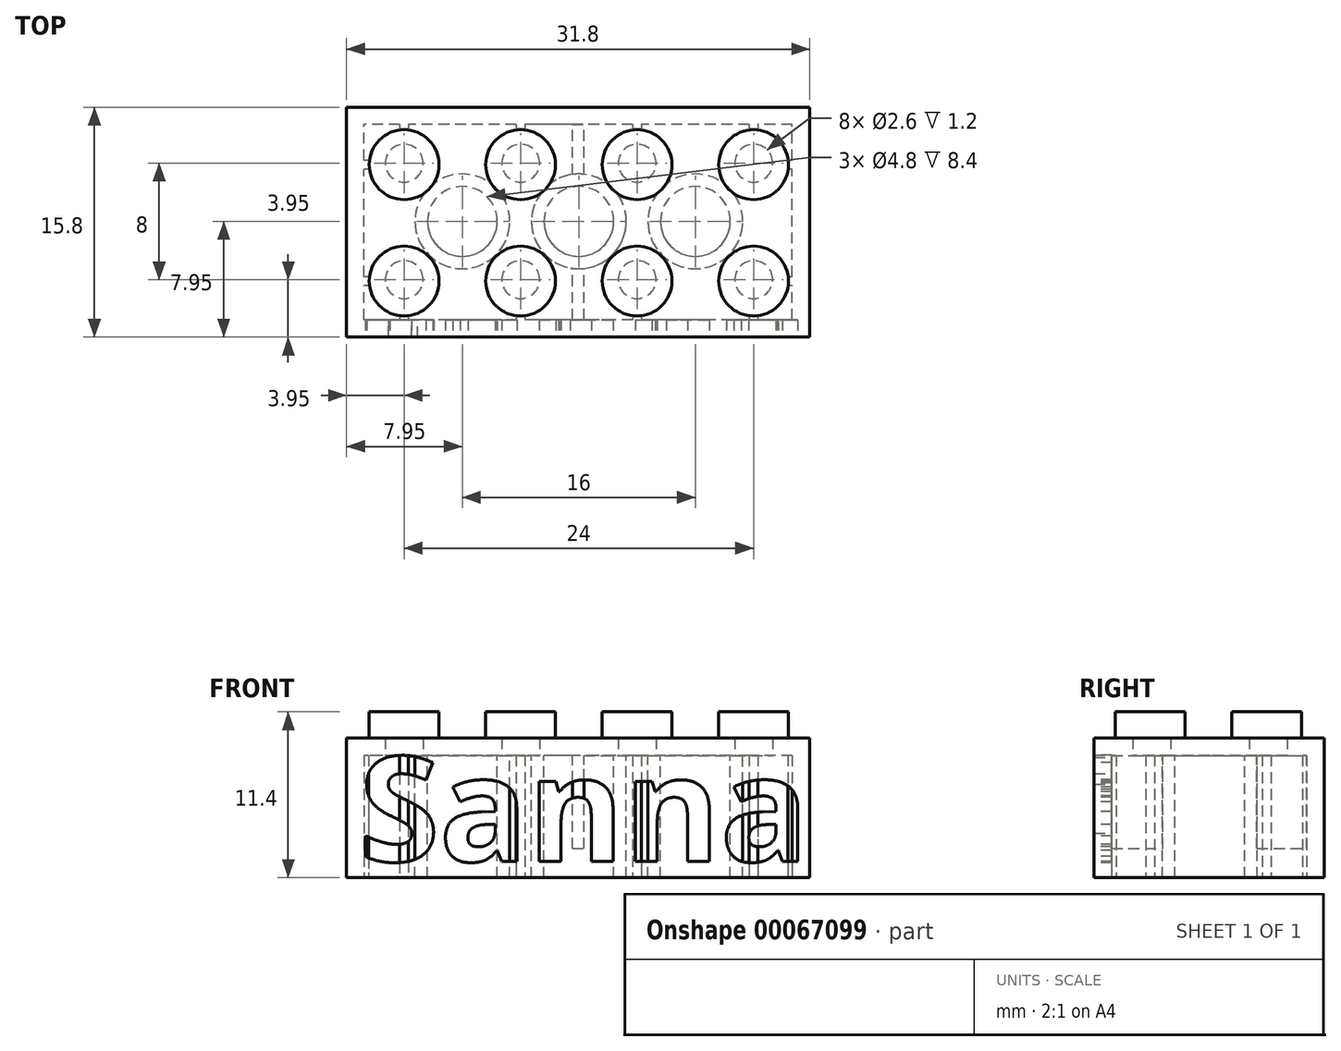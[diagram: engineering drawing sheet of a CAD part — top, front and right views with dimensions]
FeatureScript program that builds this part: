
annotation { "Feature Type Name" : "Feature", "Feature Type Description" : "" }
export const myFeature = defineFeature(function(context is Context, id is Id, definition is map)
    precondition{}
    {
        {
            var Q0;
            Q0=qCreatedBy(makeId("Top.planeOp"),FACE);
            var sketch = newSketch(context, id + "F0", { "sketchPlane" : qUnion([Q0])});
            skLineSegment(sketch, "E0.rect.bottom", {"start": v(15.9, 7.9) * mm, "end": v(-15.9, 7.9) * mm});
            skLineSegment(sketch, "E0.rect.top", {"start": v(15.9, -7.9) * mm, "end": v(-15.9, -7.9) * mm});
            skLineSegment(sketch, "E0.rect.left", {"start": v(15.9, 7.9) * mm, "end": v(15.9, -7.9) * mm});
            skLineSegment(sketch, "E0.rect.right", {"start": v(-15.9, 7.9) * mm, "end": v(-15.9, -7.9) * mm});
            skPoint(sketch, "E0.rect.middle", {"position": v(0, 0) * mm});
            skSolve(sketch);
        }
        {
            var Q0;
            Q0 = qSketchRegion(id + "F0", true);
            extrude(context, id + "F1", {"entities" : qUnion([Q0]), "depth" : 9.6 * mm});
        }
        {
            var Q0;
            Q0=makeQuery(id+"F1.opExtrude","CAP_FACE",FACE,{"disambiguationData":[OSD([sQuery(id+"F0.wireOp",EDGE,"E0.rect.bottom"),sQuery(id+"F0.wireOp",EDGE,"E0.rect.top"),sQuery(id+"F0.wireOp",EDGE,"E0.rect.left"),sQuery(id+"F0.wireOp",EDGE,"E0.rect.right")])],"isStart":true});
            var sketch = newSketch(context, id + "F2", { "sketchPlane" : qUnion([Q0])});
            skLineSegment(sketch, "E1.rect.bottom", {"start": v(14.7, 6.7) * mm, "end": v(-14.7, 6.7) * mm});
            skLineSegment(sketch, "E1.rect.top", {"start": v(14.7, -6.7) * mm, "end": v(-14.7, -6.7) * mm});
            skLineSegment(sketch, "E1.rect.left", {"start": v(14.7, 6.7) * mm, "end": v(14.7, -6.7) * mm});
            skLineSegment(sketch, "E1.rect.right", {"start": v(-14.7, 6.7) * mm, "end": v(-14.7, -6.7) * mm});
            skPoint(sketch, "E1.rect.middle", {"position": v(0, 0) * mm});
            skSolve(sketch);
        }
        {
            var Q0;
            Q0 = qSketchRegion(id + "F2", true);
            extrude(context, id + "F3", {"entities" : qUnion([Q0]), "operationType" : NewBodyOperationType.REMOVE, "oppositeDirection" : true, "depth" : 8.4 * mm});
        }
        {
            var Q0;
            Q0=makeQuery(id+"F1.opExtrude","CAP_FACE",FACE,{"disambiguationData":[OSD([sQuery(id+"F0.wireOp",EDGE,"E0.rect.bottom"),sQuery(id+"F0.wireOp",EDGE,"E0.rect.top"),sQuery(id+"F0.wireOp",EDGE,"E0.rect.left"),sQuery(id+"F0.wireOp",EDGE,"E0.rect.right")])],"isStart":false});
            var sketch = newSketch(context, id + "F4", { "sketchPlane" : qUnion([Q0])});
            skCircle(sketch, "E2", {"center": v(-11.95, 3.95) * mm, "radius": 2.4 * mm});
            skCircle(sketch, "E3.0.1.0", {"center": v(-11.95, -4.05) * mm, "radius": 2.4 * mm});
            skCircle(sketch, "E3.1.0.0", {"center": v(-3.95, 3.95) * mm, "radius": 2.4 * mm});
            skCircle(sketch, "E3.1.1.0", {"center": v(-3.95, -4.05) * mm, "radius": 2.4 * mm});
            skCircle(sketch, "E3.2.0.0", {"center": v(4.05, 3.95) * mm, "radius": 2.4 * mm});
            skCircle(sketch, "E3.2.1.0", {"center": v(4.05, -4.05) * mm, "radius": 2.4 * mm});
            skCircle(sketch, "E3.3.0.0", {"center": v(12.05, 3.95) * mm, "radius": 2.4 * mm});
            skCircle(sketch, "E3.3.1.0", {"center": v(12.05, -4.05) * mm, "radius": 2.4 * mm});
            skLineSegment(sketch, "E3.direction1", {"start": v(-11.95, 3.95) * mm, "end": v(-3.95, 3.95) * mm, "construction": true});
            skLineSegment(sketch, "E3.direction2", {"start": v(-11.95, 3.95) * mm, "end": v(-11.95, -4.05) * mm, "construction": true});
            skLineSegment(sketch, "E4", {"start": v(-23.88, 0) * mm, "end": v(20.47, 0) * mm, "construction": true});
            skSolve(sketch);
        }
        {
            var Q0;
            Q0 = qSketchRegion(id + "F4", true);
            extrude(context, id + "F5", {"entities" : qUnion([Q0]), "operationType" : NewBodyOperationType.ADD, "depth" : 1.8 * mm});
        }
        {
            var Q0;
            Q0=makeQuery(id+"F3.boolean.opBoolean","COPY",FACE,{"derivedFrom":makeQuery(id+"F3.opExtrude","CAP_FACE",FACE,{"disambiguationData":[OSD([sQuery(id+"F2.wireOp",EDGE,"E1.rect.bottom"),sQuery(id+"F2.wireOp",EDGE,"E1.rect.top"),sQuery(id+"F2.wireOp",EDGE,"E1.rect.left"),sQuery(id+"F2.wireOp",EDGE,"E1.rect.right")])],"isStart":false})});
            var sketch = newSketch(context, id + "F6", { "sketchPlane" : qUnion([Q0])});
            skCircle(sketch, "E5", {"center": v(-11.95, 3.95) * mm, "radius": 1.3 * mm});
            skCircle(sketch, "E6.0.1.0", {"center": v(-11.95, -4.05) * mm, "radius": 1.3 * mm});
            skCircle(sketch, "E6.1.0.0", {"center": v(-3.95, 3.95) * mm, "radius": 1.3 * mm});
            skCircle(sketch, "E6.1.1.0", {"center": v(-3.95, -4.05) * mm, "radius": 1.3 * mm});
            skCircle(sketch, "E6.2.0.0", {"center": v(4.05, 3.95) * mm, "radius": 1.3 * mm});
            skCircle(sketch, "E6.2.1.0", {"center": v(4.05, -4.05) * mm, "radius": 1.3 * mm});
            skCircle(sketch, "E6.3.0.0", {"center": v(12.05, 3.95) * mm, "radius": 1.3 * mm});
            skCircle(sketch, "E6.3.1.0", {"center": v(12.05, -4.05) * mm, "radius": 1.3 * mm});
            skLineSegment(sketch, "E6.direction1", {"start": v(-11.95, 3.95) * mm, "end": v(-3.95, 3.95) * mm, "construction": true});
            skLineSegment(sketch, "E6.direction2", {"start": v(-11.95, 3.95) * mm, "end": v(-11.95, -4.05) * mm, "construction": true});
            skSolve(sketch);
        }
        {
            var Q0;
            Q0 = qSketchRegion(id + "F6", true);
            extrude(context, id + "F7", {"entities" : qUnion([Q0]), "operationType" : NewBodyOperationType.REMOVE, "oppositeDirection" : true, "depth" : 1.2 * mm});
        }
        {
            var Q0;
            Q0=makeQuery(id+"F3.boolean.opBoolean","COPY",FACE,{"derivedFrom":makeQuery(id+"F3.opExtrude","CAP_FACE",FACE,{"disambiguationData":[OSD([sQuery(id+"F2.wireOp",EDGE,"E1.rect.bottom"),sQuery(id+"F2.wireOp",EDGE,"E1.rect.top"),sQuery(id+"F2.wireOp",EDGE,"E1.rect.left"),sQuery(id+"F2.wireOp",EDGE,"E1.rect.right")])],"isStart":false})});
            var sketch = newSketch(context, id + "F8", { "sketchPlane" : qUnion([Q0])});
            skLineSegment(sketch, "E7", {"start": v(-3.95, 3.95) * mm, "end": v(-11.95, -4.05) * mm, "construction": true});
            skLineSegment(sketch, "E8", {"start": v(-3.95, 3.95) * mm, "end": v(4.05, -4.05) * mm, "construction": true});
            skLineSegment(sketch, "E9", {"start": v(4.05, 3.95) * mm, "end": v(-3.95, -4.05) * mm, "construction": true});
            skLineSegment(sketch, "E10", {"start": v(4.05, 3.95) * mm, "end": v(12.05, -4.05) * mm, "construction": true});
            skLineSegment(sketch, "E11", {"start": v(12.05, 3.95) * mm, "end": v(4.05, -4.05) * mm, "construction": true});
            skLineSegment(sketch, "E12", {"start": v(-3.95, -4.05) * mm, "end": v(-11.95, 3.95) * mm, "construction": true});
            skCircle(sketch, "E13", {"center": v(-7.95, -0.05) * mm, "radius": 3.25 * mm});
            skCircle(sketch, "E14", {"center": v(-7.95, -0.05) * mm, "radius": 2.4 * mm});
            skCircle(sketch, "E15", {"center": v(0.05, -0.05) * mm, "radius": 3.25 * mm});
            skCircle(sketch, "E16", {"center": v(0.05, -0.05) * mm, "radius": 2.4 * mm});
            skCircle(sketch, "E17", {"center": v(8.05, -0.05) * mm, "radius": 3.25 * mm});
            skCircle(sketch, "E18", {"center": v(8.05, -0.05) * mm, "radius": 2.4 * mm});
            skSolve(sketch);
        }
        {
            var Q0;
            Q0 = qSketchRegion(id + "F8", true);
            var Q1;
            Q1=makeQuery(id+"F1.opExtrude","CAP_FACE",FACE,{"disambiguationData":[OSD([sQuery(id+"F0.wireOp",EDGE,"E0.rect.bottom"),sQuery(id+"F0.wireOp",EDGE,"E0.rect.top"),sQuery(id+"F0.wireOp",EDGE,"E0.rect.left"),sQuery(id+"F0.wireOp",EDGE,"E0.rect.right")])],"isStart":true});
            extrude(context, id + "F9", {"entities" : qUnion([Q0]), "operationType" : NewBodyOperationType.ADD, "endBound" : BoundingType.UP_TO_SURFACE, "endBoundEntityFace" : qUnion([Q1]), "depth" : 25 * mm});
        }
        {
            var Q0;
            Q0=makeQuery(id+"F1.opExtrude","CAP_FACE",FACE,{"disambiguationData":[OSD([sQuery(id+"F0.wireOp",EDGE,"E0.rect.bottom"),sQuery(id+"F0.wireOp",EDGE,"E0.rect.top"),sQuery(id+"F0.wireOp",EDGE,"E0.rect.left"),sQuery(id+"F0.wireOp",EDGE,"E0.rect.right")])],"isStart":true});
            var sketch = newSketch(context, id + "F10", { "sketchPlane" : qUnion([Q0])});
            skLineSegment(sketch, "E19.bottom", {"start": v(-12.25, 6.7) * mm, "end": v(-11.65, 6.7) * mm});
            skLineSegment(sketch, "E19.top", {"start": v(-12.25, 6.4) * mm, "end": v(-11.65, 6.4) * mm});
            skLineSegment(sketch, "E19.left", {"start": v(-12.25, 6.7) * mm, "end": v(-12.25, 6.4) * mm});
            skLineSegment(sketch, "E19.right", {"start": v(-11.65, 6.7) * mm, "end": v(-11.65, 6.4) * mm});
            skLineSegment(sketch, "E20", {"start": v(-11.95, 23.96) * mm, "end": v(-11.95, -3.95) * mm, "construction": true});
            skLineSegment(sketch, "E21.0.1.0", {"start": v(-11.65, -6.4) * mm, "end": v(-11.65, -6.7) * mm});
            skLineSegment(sketch, "E21.0.1.1", {"start": v(-12.25, -6.4) * mm, "end": v(-11.65, -6.4) * mm});
            skLineSegment(sketch, "E21.0.1.2", {"start": v(-12.25, -6.4) * mm, "end": v(-12.25, -6.7) * mm});
            skLineSegment(sketch, "E21.0.1.3", {"start": v(-12.25, -6.7) * mm, "end": v(-11.65, -6.7) * mm});
            skLineSegment(sketch, "E21.1.0.0", {"start": v(-3.65, 6.7) * mm, "end": v(-3.65, 6.4) * mm});
            skLineSegment(sketch, "E21.1.0.1", {"start": v(-4.25, 6.7) * mm, "end": v(-3.65, 6.7) * mm});
            skLineSegment(sketch, "E21.1.0.2", {"start": v(-4.25, 6.7) * mm, "end": v(-4.25, 6.4) * mm});
            skLineSegment(sketch, "E21.1.0.3", {"start": v(-4.25, 6.4) * mm, "end": v(-3.65, 6.4) * mm});
            skLineSegment(sketch, "E21.1.1.0", {"start": v(-3.65, -6.4) * mm, "end": v(-3.65, -6.7) * mm});
            skLineSegment(sketch, "E21.1.1.1", {"start": v(-4.25, -6.4) * mm, "end": v(-3.65, -6.4) * mm});
            skLineSegment(sketch, "E21.1.1.2", {"start": v(-4.25, -6.4) * mm, "end": v(-4.25, -6.7) * mm});
            skLineSegment(sketch, "E21.1.1.3", {"start": v(-4.25, -6.7) * mm, "end": v(-3.65, -6.7) * mm});
            skLineSegment(sketch, "E21.2.0.0", {"start": v(4.35, 6.7) * mm, "end": v(4.35, 6.4) * mm});
            skLineSegment(sketch, "E21.2.0.1", {"start": v(3.75, 6.7) * mm, "end": v(4.35, 6.7) * mm});
            skLineSegment(sketch, "E21.2.0.2", {"start": v(3.75, 6.7) * mm, "end": v(3.75, 6.4) * mm});
            skLineSegment(sketch, "E21.2.0.3", {"start": v(3.75, 6.4) * mm, "end": v(4.35, 6.4) * mm});
            skLineSegment(sketch, "E21.2.1.0", {"start": v(4.35, -6.4) * mm, "end": v(4.35, -6.7) * mm});
            skLineSegment(sketch, "E21.2.1.1", {"start": v(3.75, -6.4) * mm, "end": v(4.35, -6.4) * mm});
            skLineSegment(sketch, "E21.2.1.2", {"start": v(3.75, -6.4) * mm, "end": v(3.75, -6.7) * mm});
            skLineSegment(sketch, "E21.2.1.3", {"start": v(3.75, -6.7) * mm, "end": v(4.35, -6.7) * mm});
            skLineSegment(sketch, "E21.3.0.0", {"start": v(12.35, 6.7) * mm, "end": v(12.35, 6.4) * mm});
            skLineSegment(sketch, "E21.3.0.1", {"start": v(11.75, 6.7) * mm, "end": v(12.35, 6.7) * mm});
            skLineSegment(sketch, "E21.3.0.2", {"start": v(11.75, 6.7) * mm, "end": v(11.75, 6.4) * mm});
            skLineSegment(sketch, "E21.3.0.3", {"start": v(11.75, 6.4) * mm, "end": v(12.35, 6.4) * mm});
            skLineSegment(sketch, "E21.3.1.0", {"start": v(12.35, -6.4) * mm, "end": v(12.35, -6.7) * mm});
            skLineSegment(sketch, "E21.3.1.1", {"start": v(11.75, -6.4) * mm, "end": v(12.35, -6.4) * mm});
            skLineSegment(sketch, "E21.3.1.2", {"start": v(11.75, -6.4) * mm, "end": v(11.75, -6.7) * mm});
            skLineSegment(sketch, "E21.3.1.3", {"start": v(11.75, -6.7) * mm, "end": v(12.35, -6.7) * mm});
            skLineSegment(sketch, "E21.direction1", {"start": v(-11.65, 6.4) * mm, "end": v(-3.65, 6.4) * mm, "construction": true});
            skLineSegment(sketch, "E21.direction2", {"start": v(-11.65, 6.4) * mm, "end": v(-11.65, -6.7) * mm, "construction": true});
            skSolve(sketch);
        }
        {
            var Q0;
            Q0 = qSketchRegion(id + "F10", true);
            var Q1;
            {var subQ0=sQuery(id+"F2.wireOp",EDGE,"E1.rect.bottom");var subQ1=sQuery(id+"F2.wireOp",EDGE,"E1.rect.top");var subQ2=sQuery(id+"F2.wireOp",EDGE,"E1.rect.left");var subQ3=sQuery(id+"F2.wireOp",EDGE,"E1.rect.right");Q1=makeQuery(id+"F9.boolean.opBoolean","SPLIT",FACE,{"disambiguationData":[TD([makeQuery(id+"F3.boolean.opBoolean","COPY",FACE,{"derivedFrom":makeQuery(id+"F3.opExtrude","SWEPT_FACE",FACE,{"disambiguationData":[OSD([subQ0])]})})])],"derivedFrom":makeQuery(id+"F3.boolean.opBoolean","COPY",FACE,{"derivedFrom":makeQuery(id+"F3.opExtrude","CAP_FACE",FACE,{"disambiguationData":[OSD([subQ0,subQ1,subQ2,subQ3])],"isStart":false})})});}
            extrude(context, id + "F11", {"entities" : qUnion([Q0]), "operationType" : NewBodyOperationType.ADD, "endBound" : BoundingType.UP_TO_SURFACE, "oppositeDirection" : true, "endBoundEntityFace" : qUnion([Q1]), "depth" : 25 * mm});
        }
        {
            var Q0;
            Q0=qCreatedBy(makeId("Top.planeOp"),FACE);
            var sketch = newSketch(context, id + "F12", { "sketchPlane" : qUnion([Q0])});
            skLineSegment(sketch, "E22.bottom", {"start": v(-14.7, -4.35) * mm, "end": v(-14.4, -4.35) * mm});
            skLineSegment(sketch, "E22.top", {"start": v(-14.7, -3.75) * mm, "end": v(-14.4, -3.75) * mm});
            skLineSegment(sketch, "E22.left", {"start": v(-14.7, -4.35) * mm, "end": v(-14.7, -3.75) * mm});
            skLineSegment(sketch, "E22.right", {"start": v(-14.4, -4.35) * mm, "end": v(-14.4, -3.75) * mm});
            skLineSegment(sketch, "E23", {"start": v(-14.7, -4.05) * mm, "end": v(12.05, -4.05) * mm, "construction": true});
            skLineSegment(sketch, "E24.0.1.0", {"start": v(-14.4, 3.65) * mm, "end": v(-14.4, 4.25) * mm});
            skLineSegment(sketch, "E24.0.1.1", {"start": v(-14.7, 3.65) * mm, "end": v(-14.4, 3.65) * mm});
            skLineSegment(sketch, "E24.0.1.2", {"start": v(-14.7, 3.65) * mm, "end": v(-14.7, 4.25) * mm});
            skLineSegment(sketch, "E24.0.1.3", {"start": v(-14.7, 4.25) * mm, "end": v(-14.4, 4.25) * mm});
            skLineSegment(sketch, "E24.1.0.0", {"start": v(14.7, -4.35) * mm, "end": v(14.7, -3.75) * mm});
            skLineSegment(sketch, "E24.1.0.1", {"start": v(14.4, -4.35) * mm, "end": v(14.7, -4.35) * mm});
            skLineSegment(sketch, "E24.1.0.2", {"start": v(14.4, -4.35) * mm, "end": v(14.4, -3.75) * mm});
            skLineSegment(sketch, "E24.1.0.3", {"start": v(14.4, -3.75) * mm, "end": v(14.7, -3.75) * mm});
            skLineSegment(sketch, "E24.1.1.0", {"start": v(14.7, 3.65) * mm, "end": v(14.7, 4.25) * mm});
            skLineSegment(sketch, "E24.1.1.1", {"start": v(14.4, 3.65) * mm, "end": v(14.7, 3.65) * mm});
            skLineSegment(sketch, "E24.1.1.2", {"start": v(14.4, 3.65) * mm, "end": v(14.4, 4.25) * mm});
            skLineSegment(sketch, "E24.1.1.3", {"start": v(14.4, 4.25) * mm, "end": v(14.7, 4.25) * mm});
            skLineSegment(sketch, "E24.direction1", {"start": v(-14.4, -4.35) * mm, "end": v(14.7, -4.35) * mm, "construction": true});
            skLineSegment(sketch, "E24.direction2", {"start": v(-14.4, -4.35) * mm, "end": v(-14.4, 3.65) * mm, "construction": true});
            skSolve(sketch);
        }
        {
            var Q0;
            Q0 = qSketchRegion(id + "F12", true);
            var Q1;
            {var subQ0=sQuery(id+"F2.wireOp",EDGE,"E1.rect.bottom");var subQ1=sQuery(id+"F2.wireOp",EDGE,"E1.rect.top");var subQ2=sQuery(id+"F2.wireOp",EDGE,"E1.rect.left");var subQ3=sQuery(id+"F2.wireOp",EDGE,"E1.rect.right");Q1=makeQuery(id+"F9.boolean.opBoolean","SPLIT",FACE,{"disambiguationData":[TD([makeQuery(id+"F3.boolean.opBoolean","COPY",FACE,{"derivedFrom":makeQuery(id+"F3.opExtrude","SWEPT_FACE",FACE,{"disambiguationData":[OSD([subQ0])]})})])],"derivedFrom":makeQuery(id+"F3.boolean.opBoolean","COPY",FACE,{"derivedFrom":makeQuery(id+"F3.opExtrude","CAP_FACE",FACE,{"disambiguationData":[OSD([subQ0,subQ1,subQ2,subQ3])],"isStart":false})})});}
            extrude(context, id + "F13", {"entities" : qUnion([Q0]), "operationType" : NewBodyOperationType.ADD, "endBound" : BoundingType.UP_TO_SURFACE, "endBoundEntityFace" : qUnion([Q1]), "depth" : 25 * mm});
        }
        {
            var Q0;
            {var subQ0=sQuery(id+"F2.wireOp",EDGE,"E1.rect.bottom");var subQ1=sQuery(id+"F2.wireOp",EDGE,"E1.rect.top");var subQ2=sQuery(id+"F2.wireOp",EDGE,"E1.rect.left");var subQ3=sQuery(id+"F2.wireOp",EDGE,"E1.rect.right");Q0=makeQuery(id+"F9.boolean.opBoolean","SPLIT",FACE,{"disambiguationData":[TD([makeQuery(id+"F3.boolean.opBoolean","COPY",FACE,{"derivedFrom":makeQuery(id+"F3.opExtrude","SWEPT_FACE",FACE,{"disambiguationData":[OSD([subQ0])]})})])],"derivedFrom":makeQuery(id+"F3.boolean.opBoolean","COPY",FACE,{"derivedFrom":makeQuery(id+"F3.opExtrude","CAP_FACE",FACE,{"disambiguationData":[OSD([subQ0,subQ1,subQ2,subQ3])],"isStart":false})})});}
            var sketch = newSketch(context, id + "F14", { "sketchPlane" : qUnion([Q0])});
            skLineSegment(sketch, "E25.bottom", {"start": v(-0.4, 6.9) * mm, "end": v(0.4, 6.9) * mm});
            skLineSegment(sketch, "E25.top", {"start": v(-0.4, 3) * mm, "end": v(0.4, 3) * mm});
            skLineSegment(sketch, "E25.left", {"start": v(-0.4, 6.9) * mm, "end": v(-0.4, 3) * mm});
            skLineSegment(sketch, "E25.right", {"start": v(0.4, 6.9) * mm, "end": v(0.4, 3) * mm});
            skLineSegment(sketch, "E26", {"start": v(0, 9.73) * mm, "end": v(0, -10.53) * mm, "construction": true});
            skLineSegment(sketch, "E27.bottom", {"start": v(-0.4, -3.1) * mm, "end": v(0.4, -3.1) * mm});
            skLineSegment(sketch, "E27.top", {"start": v(-0.4, -6.9) * mm, "end": v(0.4, -6.9) * mm});
            skLineSegment(sketch, "E27.left", {"start": v(-0.4, -3.1) * mm, "end": v(-0.4, -6.9) * mm});
            skLineSegment(sketch, "E27.right", {"start": v(0.4, -3.1) * mm, "end": v(0.4, -6.9) * mm});
            skSolve(sketch);
        }
        {
            var Q0;
            Q0 = qSketchRegion(id + "F14", true);
            extrude(context, id + "F15", {"entities" : qUnion([Q0]), "operationType" : NewBodyOperationType.ADD, "depth" : 6.4 * mm});
        }
        {
            var Q0;
            Q0=makeQuery(id+"F1.opExtrude","SWEPT_FACE",FACE,{"disambiguationData":[OSD([sQuery(id+"F0.wireOp",EDGE,"E0.rect.top")])]});
            var sketch = newSketch(context, id + "F16", { "sketchPlane" : qUnion([Q0])});
            skText(sketch, "E28", { "text": "Sanna", "fontName": "OpenSans-Bold.ttf"});
            const initialGuessF16  = {"E28": [-0.01507, 0.00113, 1, 0, 0.00724]};
            skSetInitialGuess(sketch, initialGuessF16);
            skSolve(sketch);
        }
        {
            var Q0;
            Q0 = qSketchRegion(id + "F16", true);
            extrude(context, id + "F17", {"entities" : qUnion([Q0]), "operationType" : NewBodyOperationType.REMOVE, "oppositeDirection" : true, "depth" : 1.2 * mm});
        }
    });
